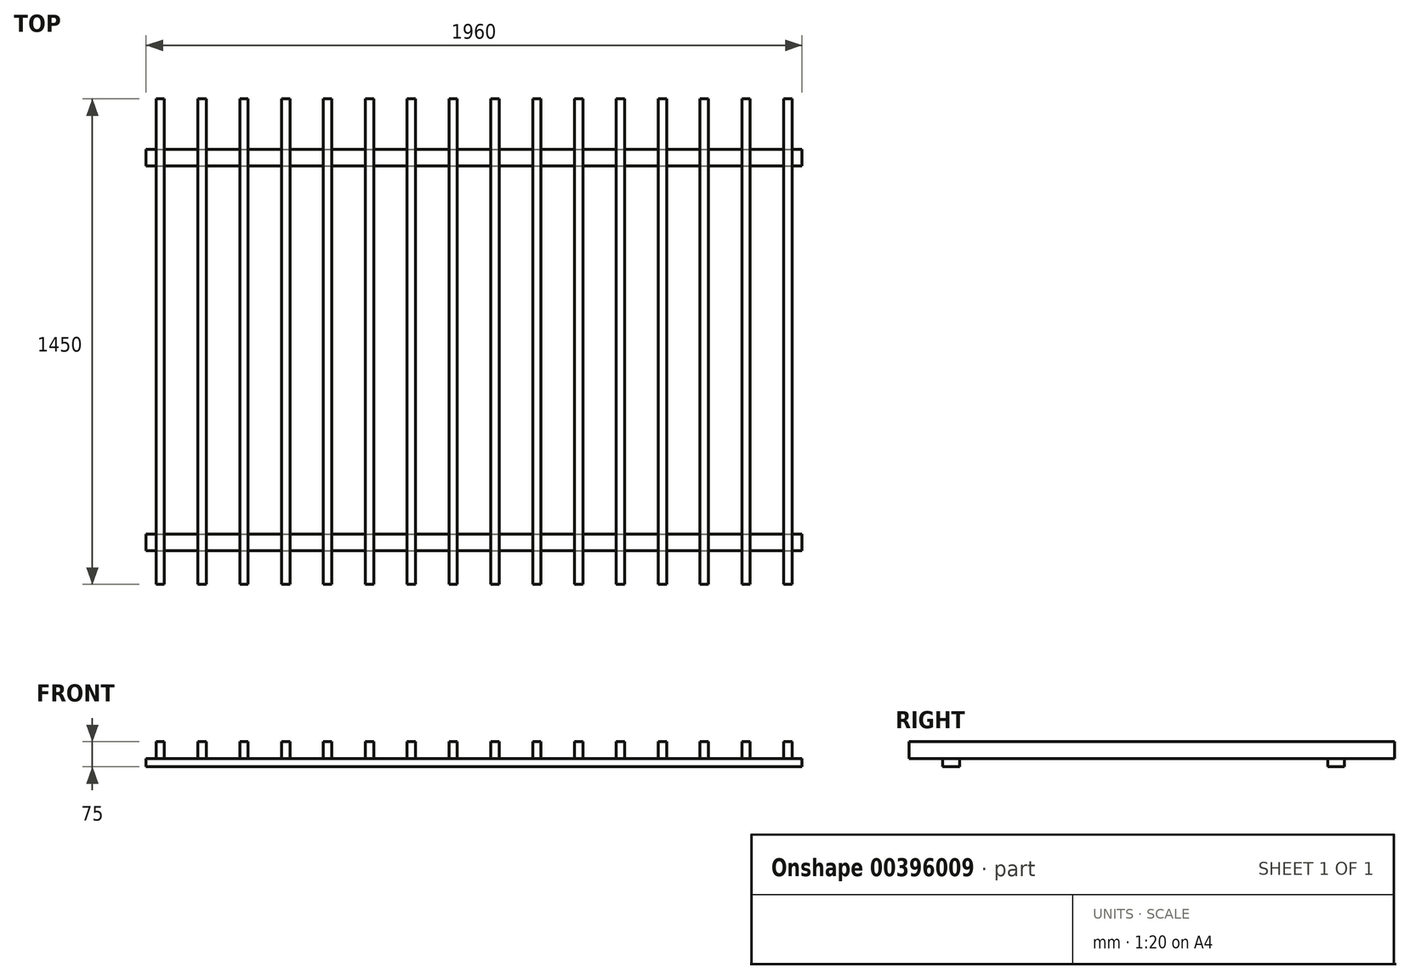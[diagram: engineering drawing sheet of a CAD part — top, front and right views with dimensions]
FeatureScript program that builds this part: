
annotation { "Feature Type Name" : "Feature", "Feature Type Description" : "" }
export const myFeature = defineFeature(function(context is Context, id is Id, definition is map)
    precondition{}
    {
        {
            var Q0;
            Q0=qCreatedBy(makeId("Top.planeOp"),FACE);
            var sketch = newSketch(context, id + "F0", { "sketchPlane" : qUnion([Q0])});
            skLineSegment(sketch, "E0.bottom", {"start": v(0, 0) * mm, "end": v(1960, 0) * mm, "construction": true});
            skLineSegment(sketch, "E0.top", {"start": v(0, 1500) * mm, "end": v(1960, 1500) * mm, "construction": true});
            skLineSegment(sketch, "E0.left", {"start": v(0, 0) * mm, "end": v(0, 1500) * mm, "construction": true});
            skLineSegment(sketch, "E0.right", {"start": v(1960, 0) * mm, "end": v(1960, 1500) * mm, "construction": true});
            skLineSegment(sketch, "E1.bottom", {"start": v(0, 150) * mm, "end": v(1960, 150) * mm});
            skLineSegment(sketch, "E1.top", {"start": v(0, 175) * mm, "end": v(1960, 175) * mm});
            skLineSegment(sketch, "E1.left", {"start": v(0, 150) * mm, "end": v(0, 175) * mm});
            skLineSegment(sketch, "E1.right", {"start": v(1960, 150) * mm, "end": v(1960, 175) * mm});
            skLineSegment(sketch, "E2", {"start": v(0, 750) * mm, "end": v(1960, 750) * mm, "construction": true});
            skLineSegment(sketch, "E3.MirrorCS", {"start": v(1960, 1350) * mm, "end": v(1960, 1325) * mm});
            skLineSegment(sketch, "E4.MirrorCS", {"start": v(0, 1350) * mm, "end": v(0, 1325) * mm});
            skLineSegment(sketch, "E5.MirrorCS", {"start": v(0, 1350) * mm, "end": v(1960, 1350) * mm});
            skLineSegment(sketch, "E6.MirrorCS", {"start": v(0, 1325) * mm, "end": v(1960, 1325) * mm});
            skLineSegment(sketch, "E7.bottom", {"start": v(30, 1500) * mm, "end": v(55, 1500) * mm});
            skLineSegment(sketch, "E7.top", {"start": v(30, 50) * mm, "end": v(55, 50) * mm});
            skLineSegment(sketch, "E7.left", {"start": v(30, 1500) * mm, "end": v(30, 50) * mm});
            skLineSegment(sketch, "E7.right", {"start": v(55, 1500) * mm, "end": v(55, 50) * mm});
            skLineSegment(sketch, "E8.1.0.0", {"start": v(155, 1500) * mm, "end": v(155, 50) * mm});
            skLineSegment(sketch, "E8.1.0.1", {"start": v(180, 1500) * mm, "end": v(180, 50) * mm});
            skLineSegment(sketch, "E8.1.0.2", {"start": v(155, 1500) * mm, "end": v(180, 1500) * mm});
            skLineSegment(sketch, "E8.1.0.3", {"start": v(155, 50) * mm, "end": v(180, 50) * mm});
            skLineSegment(sketch, "E8.2.0.0", {"start": v(280, 1500) * mm, "end": v(280, 50) * mm});
            skLineSegment(sketch, "E8.2.0.1", {"start": v(305, 1500) * mm, "end": v(305, 50) * mm});
            skLineSegment(sketch, "E8.2.0.2", {"start": v(280, 1500) * mm, "end": v(305, 1500) * mm});
            skLineSegment(sketch, "E8.2.0.3", {"start": v(280, 50) * mm, "end": v(305, 50) * mm});
            skLineSegment(sketch, "E8.3.0.0", {"start": v(405, 1500) * mm, "end": v(405, 50) * mm});
            skLineSegment(sketch, "E8.3.0.1", {"start": v(430, 1500) * mm, "end": v(430, 50) * mm});
            skLineSegment(sketch, "E8.3.0.2", {"start": v(405, 1500) * mm, "end": v(430, 1500) * mm});
            skLineSegment(sketch, "E8.3.0.3", {"start": v(405, 50) * mm, "end": v(430, 50) * mm});
            skLineSegment(sketch, "E8.4.0.0", {"start": v(530, 1500) * mm, "end": v(530, 50) * mm});
            skLineSegment(sketch, "E8.4.0.1", {"start": v(555, 1500) * mm, "end": v(555, 50) * mm});
            skLineSegment(sketch, "E8.4.0.2", {"start": v(530, 1500) * mm, "end": v(555, 1500) * mm});
            skLineSegment(sketch, "E8.4.0.3", {"start": v(530, 50) * mm, "end": v(555, 50) * mm});
            skLineSegment(sketch, "E8.5.0.0", {"start": v(655, 1500) * mm, "end": v(655, 50) * mm});
            skLineSegment(sketch, "E8.5.0.1", {"start": v(680, 1500) * mm, "end": v(680, 50) * mm});
            skLineSegment(sketch, "E8.5.0.2", {"start": v(655, 1500) * mm, "end": v(680, 1500) * mm});
            skLineSegment(sketch, "E8.5.0.3", {"start": v(655, 50) * mm, "end": v(680, 50) * mm});
            skLineSegment(sketch, "E8.6.0.0", {"start": v(780, 1500) * mm, "end": v(780, 50) * mm});
            skLineSegment(sketch, "E8.6.0.1", {"start": v(805, 1500) * mm, "end": v(805, 50) * mm});
            skLineSegment(sketch, "E8.6.0.2", {"start": v(780, 1500) * mm, "end": v(805, 1500) * mm});
            skLineSegment(sketch, "E8.6.0.3", {"start": v(780, 50) * mm, "end": v(805, 50) * mm});
            skLineSegment(sketch, "E8.7.0.0", {"start": v(905, 1500) * mm, "end": v(905, 50) * mm});
            skLineSegment(sketch, "E8.7.0.1", {"start": v(930, 1500) * mm, "end": v(930, 50) * mm});
            skLineSegment(sketch, "E8.7.0.2", {"start": v(905, 1500) * mm, "end": v(930, 1500) * mm});
            skLineSegment(sketch, "E8.7.0.3", {"start": v(905, 50) * mm, "end": v(930, 50) * mm});
            skLineSegment(sketch, "E8.8.0.0", {"start": v(1030, 1500) * mm, "end": v(1030, 50) * mm});
            skLineSegment(sketch, "E8.8.0.1", {"start": v(1055, 1500) * mm, "end": v(1055, 50) * mm});
            skLineSegment(sketch, "E8.8.0.2", {"start": v(1030, 1500) * mm, "end": v(1055, 1500) * mm});
            skLineSegment(sketch, "E8.8.0.3", {"start": v(1030, 50) * mm, "end": v(1055, 50) * mm});
            skLineSegment(sketch, "E8.9.0.0", {"start": v(1155, 1500) * mm, "end": v(1155, 50) * mm});
            skLineSegment(sketch, "E8.9.0.1", {"start": v(1180, 1500) * mm, "end": v(1180, 50) * mm});
            skLineSegment(sketch, "E8.9.0.2", {"start": v(1155, 1500) * mm, "end": v(1180, 1500) * mm});
            skLineSegment(sketch, "E8.9.0.3", {"start": v(1155, 50) * mm, "end": v(1180, 50) * mm});
            skLineSegment(sketch, "E8.10.0.0", {"start": v(1280, 1500) * mm, "end": v(1280, 50) * mm});
            skLineSegment(sketch, "E8.10.0.1", {"start": v(1305, 1500) * mm, "end": v(1305, 50) * mm});
            skLineSegment(sketch, "E8.10.0.2", {"start": v(1280, 1500) * mm, "end": v(1305, 1500) * mm});
            skLineSegment(sketch, "E8.10.0.3", {"start": v(1280, 50) * mm, "end": v(1305, 50) * mm});
            skLineSegment(sketch, "E8.11.0.0", {"start": v(1405, 1500) * mm, "end": v(1405, 50) * mm});
            skLineSegment(sketch, "E8.11.0.1", {"start": v(1430, 1500) * mm, "end": v(1430, 50) * mm});
            skLineSegment(sketch, "E8.11.0.2", {"start": v(1405, 1500) * mm, "end": v(1430, 1500) * mm});
            skLineSegment(sketch, "E8.11.0.3", {"start": v(1405, 50) * mm, "end": v(1430, 50) * mm});
            skLineSegment(sketch, "E8.12.0.0", {"start": v(1530, 1500) * mm, "end": v(1530, 50) * mm});
            skLineSegment(sketch, "E8.12.0.1", {"start": v(1555, 1500) * mm, "end": v(1555, 50) * mm});
            skLineSegment(sketch, "E8.12.0.2", {"start": v(1530, 1500) * mm, "end": v(1555, 1500) * mm});
            skLineSegment(sketch, "E8.12.0.3", {"start": v(1530, 50) * mm, "end": v(1555, 50) * mm});
            skLineSegment(sketch, "E8.13.0.0", {"start": v(1655, 1500) * mm, "end": v(1655, 50) * mm});
            skLineSegment(sketch, "E8.13.0.1", {"start": v(1680, 1500) * mm, "end": v(1680, 50) * mm});
            skLineSegment(sketch, "E8.13.0.2", {"start": v(1655, 1500) * mm, "end": v(1680, 1500) * mm});
            skLineSegment(sketch, "E8.13.0.3", {"start": v(1655, 50) * mm, "end": v(1680, 50) * mm});
            skLineSegment(sketch, "E8.14.0.0", {"start": v(1780, 1500) * mm, "end": v(1780, 50) * mm});
            skLineSegment(sketch, "E8.14.0.1", {"start": v(1805, 1500) * mm, "end": v(1805, 50) * mm});
            skLineSegment(sketch, "E8.14.0.2", {"start": v(1780, 1500) * mm, "end": v(1805, 1500) * mm});
            skLineSegment(sketch, "E8.14.0.3", {"start": v(1780, 50) * mm, "end": v(1805, 50) * mm});
            skLineSegment(sketch, "E8.direction1", {"start": v(30, 50) * mm, "end": v(155, 50) * mm, "construction": true});
            skLineSegment(sketch, "E9.0.15.0", {"start": v(1905, 1500) * mm, "end": v(1905, 50) * mm});
            skLineSegment(sketch, "E9.3.15.0", {"start": v(1930, 1500) * mm, "end": v(1930, 50) * mm});
            skLineSegment(sketch, "E9.6.15.0", {"start": v(1905, 1500) * mm, "end": v(1930, 1500) * mm});
            skLineSegment(sketch, "E9.9.15.0", {"start": v(1905, 50) * mm, "end": v(1930, 50) * mm});
            skSolve(sketch);
        }
        {
            var Q0;
            {var subQ5=sQuery(id+"F0.wireOp",EDGE,"E7.top");Q0=makeQuery(id+"F0.imprint","IMPRINT",FACE,{"disambiguationData":[TD([[makeQuery(id+"F0.imprint","IMPRINT",EDGE,{"derivedFrom":subQ5}),1.0]])]});}
            var Q1;
            {var subQ5=sQuery(id+"F0.wireOp",EDGE,"E8.1.0.3");Q1=makeQuery(id+"F0.imprint","IMPRINT",FACE,{"disambiguationData":[TD([[makeQuery(id+"F0.imprint","IMPRINT",EDGE,{"derivedFrom":subQ5}),1.0]])]});}
            var Q2;
            {var subQ5=sQuery(id+"F0.wireOp",EDGE,"E8.2.0.3");Q2=makeQuery(id+"F0.imprint","IMPRINT",FACE,{"disambiguationData":[TD([[makeQuery(id+"F0.imprint","IMPRINT",EDGE,{"derivedFrom":subQ5}),1.0]])]});}
            var Q3;
            {var subQ5=sQuery(id+"F0.wireOp",EDGE,"E8.3.0.3");Q3=makeQuery(id+"F0.imprint","IMPRINT",FACE,{"disambiguationData":[TD([[makeQuery(id+"F0.imprint","IMPRINT",EDGE,{"derivedFrom":subQ5}),1.0]])]});}
            var Q4;
            {var subQ5=sQuery(id+"F0.wireOp",EDGE,"E8.4.0.3");Q4=makeQuery(id+"F0.imprint","IMPRINT",FACE,{"disambiguationData":[TD([[makeQuery(id+"F0.imprint","IMPRINT",EDGE,{"derivedFrom":subQ5}),1.0]])]});}
            var Q5;
            {var subQ5=sQuery(id+"F0.wireOp",EDGE,"E8.5.0.3");Q5=makeQuery(id+"F0.imprint","IMPRINT",FACE,{"disambiguationData":[TD([[makeQuery(id+"F0.imprint","IMPRINT",EDGE,{"derivedFrom":subQ5}),1.0]])]});}
            var Q6;
            {var subQ5=sQuery(id+"F0.wireOp",EDGE,"E8.6.0.3");Q6=makeQuery(id+"F0.imprint","IMPRINT",FACE,{"disambiguationData":[TD([[makeQuery(id+"F0.imprint","IMPRINT",EDGE,{"derivedFrom":subQ5}),1.0]])]});}
            var Q7;
            {var subQ5=sQuery(id+"F0.wireOp",EDGE,"E8.7.0.3");Q7=makeQuery(id+"F0.imprint","IMPRINT",FACE,{"disambiguationData":[TD([[makeQuery(id+"F0.imprint","IMPRINT",EDGE,{"derivedFrom":subQ5}),1.0]])]});}
            var Q8;
            {var subQ5=sQuery(id+"F0.wireOp",EDGE,"E8.8.0.3");Q8=makeQuery(id+"F0.imprint","IMPRINT",FACE,{"disambiguationData":[TD([[makeQuery(id+"F0.imprint","IMPRINT",EDGE,{"derivedFrom":subQ5}),1.0]])]});}
            var Q9;
            {var subQ5=sQuery(id+"F0.wireOp",EDGE,"E8.9.0.3");Q9=makeQuery(id+"F0.imprint","IMPRINT",FACE,{"disambiguationData":[TD([[makeQuery(id+"F0.imprint","IMPRINT",EDGE,{"derivedFrom":subQ5}),1.0]])]});}
            var Q10;
            {var subQ5=sQuery(id+"F0.wireOp",EDGE,"E8.10.0.3");Q10=makeQuery(id+"F0.imprint","IMPRINT",FACE,{"disambiguationData":[TD([[makeQuery(id+"F0.imprint","IMPRINT",EDGE,{"derivedFrom":subQ5}),1.0]])]});}
            var Q11;
            {var subQ5=sQuery(id+"F0.wireOp",EDGE,"E8.11.0.3");Q11=makeQuery(id+"F0.imprint","IMPRINT",FACE,{"disambiguationData":[TD([[makeQuery(id+"F0.imprint","IMPRINT",EDGE,{"derivedFrom":subQ5}),1.0]])]});}
            var Q12;
            {var subQ5=sQuery(id+"F0.wireOp",EDGE,"E8.12.0.3");Q12=makeQuery(id+"F0.imprint","IMPRINT",FACE,{"disambiguationData":[TD([[makeQuery(id+"F0.imprint","IMPRINT",EDGE,{"derivedFrom":subQ5}),1.0]])]});}
            var Q13;
            {var subQ5=sQuery(id+"F0.wireOp",EDGE,"E8.13.0.3");Q13=makeQuery(id+"F0.imprint","IMPRINT",FACE,{"disambiguationData":[TD([[makeQuery(id+"F0.imprint","IMPRINT",EDGE,{"derivedFrom":subQ5}),1.0]])]});}
            var Q14;
            {var subQ5=sQuery(id+"F0.wireOp",EDGE,"E8.14.0.3");Q14=makeQuery(id+"F0.imprint","IMPRINT",FACE,{"disambiguationData":[TD([[makeQuery(id+"F0.imprint","IMPRINT",EDGE,{"derivedFrom":subQ5}),1.0]])]});}
            var Q15;
            {var subQ5=sQuery(id+"F0.wireOp",EDGE,"E9.9.15.0");Q15=makeQuery(id+"F0.imprint","IMPRINT",FACE,{"disambiguationData":[TD([[makeQuery(id+"F0.imprint","IMPRINT",EDGE,{"derivedFrom":subQ5}),1.0]])]});}
            var Q16;
            {var subQ5=sQuery(id+"F0.wireOp",EDGE,"E7.bottom");Q16=makeQuery(id+"F0.imprint","IMPRINT",FACE,{"disambiguationData":[TD([[makeQuery(id+"F0.imprint","IMPRINT",EDGE,{"derivedFrom":subQ5}),-1.0]])]});}
            var Q17;
            {var subQ5=sQuery(id+"F0.wireOp",EDGE,"E8.1.0.2");Q17=makeQuery(id+"F0.imprint","IMPRINT",FACE,{"disambiguationData":[TD([[makeQuery(id+"F0.imprint","IMPRINT",EDGE,{"derivedFrom":subQ5}),-1.0]])]});}
            var Q18;
            {var subQ5=sQuery(id+"F0.wireOp",EDGE,"E8.2.0.2");Q18=makeQuery(id+"F0.imprint","IMPRINT",FACE,{"disambiguationData":[TD([[makeQuery(id+"F0.imprint","IMPRINT",EDGE,{"derivedFrom":subQ5}),-1.0]])]});}
            var Q19;
            {var subQ5=sQuery(id+"F0.wireOp",EDGE,"E8.3.0.2");Q19=makeQuery(id+"F0.imprint","IMPRINT",FACE,{"disambiguationData":[TD([[makeQuery(id+"F0.imprint","IMPRINT",EDGE,{"derivedFrom":subQ5}),-1.0]])]});}
            var Q20;
            {var subQ5=sQuery(id+"F0.wireOp",EDGE,"E8.4.0.2");Q20=makeQuery(id+"F0.imprint","IMPRINT",FACE,{"disambiguationData":[TD([[makeQuery(id+"F0.imprint","IMPRINT",EDGE,{"derivedFrom":subQ5}),-1.0]])]});}
            var Q21;
            {var subQ5=sQuery(id+"F0.wireOp",EDGE,"E8.5.0.2");Q21=makeQuery(id+"F0.imprint","IMPRINT",FACE,{"disambiguationData":[TD([[makeQuery(id+"F0.imprint","IMPRINT",EDGE,{"derivedFrom":subQ5}),-1.0]])]});}
            var Q22;
            {var subQ5=sQuery(id+"F0.wireOp",EDGE,"E8.6.0.2");Q22=makeQuery(id+"F0.imprint","IMPRINT",FACE,{"disambiguationData":[TD([[makeQuery(id+"F0.imprint","IMPRINT",EDGE,{"derivedFrom":subQ5}),-1.0]])]});}
            var Q23;
            {var subQ5=sQuery(id+"F0.wireOp",EDGE,"E8.7.0.2");Q23=makeQuery(id+"F0.imprint","IMPRINT",FACE,{"disambiguationData":[TD([[makeQuery(id+"F0.imprint","IMPRINT",EDGE,{"derivedFrom":subQ5}),-1.0]])]});}
            var Q24;
            {var subQ5=sQuery(id+"F0.wireOp",EDGE,"E8.8.0.2");Q24=makeQuery(id+"F0.imprint","IMPRINT",FACE,{"disambiguationData":[TD([[makeQuery(id+"F0.imprint","IMPRINT",EDGE,{"derivedFrom":subQ5}),-1.0]])]});}
            var Q25;
            {var subQ5=sQuery(id+"F0.wireOp",EDGE,"E8.9.0.2");Q25=makeQuery(id+"F0.imprint","IMPRINT",FACE,{"disambiguationData":[TD([[makeQuery(id+"F0.imprint","IMPRINT",EDGE,{"derivedFrom":subQ5}),-1.0]])]});}
            var Q26;
            {var subQ5=sQuery(id+"F0.wireOp",EDGE,"E8.10.0.2");Q26=makeQuery(id+"F0.imprint","IMPRINT",FACE,{"disambiguationData":[TD([[makeQuery(id+"F0.imprint","IMPRINT",EDGE,{"derivedFrom":subQ5}),-1.0]])]});}
            var Q27;
            {var subQ5=sQuery(id+"F0.wireOp",EDGE,"E8.11.0.2");Q27=makeQuery(id+"F0.imprint","IMPRINT",FACE,{"disambiguationData":[TD([[makeQuery(id+"F0.imprint","IMPRINT",EDGE,{"derivedFrom":subQ5}),-1.0]])]});}
            var Q28;
            {var subQ5=sQuery(id+"F0.wireOp",EDGE,"E8.12.0.2");Q28=makeQuery(id+"F0.imprint","IMPRINT",FACE,{"disambiguationData":[TD([[makeQuery(id+"F0.imprint","IMPRINT",EDGE,{"derivedFrom":subQ5}),-1.0]])]});}
            var Q29;
            {var subQ5=sQuery(id+"F0.wireOp",EDGE,"E8.13.0.2");Q29=makeQuery(id+"F0.imprint","IMPRINT",FACE,{"disambiguationData":[TD([[makeQuery(id+"F0.imprint","IMPRINT",EDGE,{"derivedFrom":subQ5}),-1.0]])]});}
            var Q30;
            {var subQ5=sQuery(id+"F0.wireOp",EDGE,"E8.14.0.2");Q30=makeQuery(id+"F0.imprint","IMPRINT",FACE,{"disambiguationData":[TD([[makeQuery(id+"F0.imprint","IMPRINT",EDGE,{"derivedFrom":subQ5}),-1.0]])]});}
            var Q31;
            {var subQ5=sQuery(id+"F0.wireOp",EDGE,"E9.6.15.0");Q31=makeQuery(id+"F0.imprint","IMPRINT",FACE,{"disambiguationData":[TD([[makeQuery(id+"F0.imprint","IMPRINT",EDGE,{"derivedFrom":subQ5}),-1.0]])]});}
            var Q32;
            {var subQ0=sQuery(id+"F0.wireOp",EDGE,"E7.left");var subQ1=sQuery(id+"F0.wireOp",EDGE,"E1.top");var subQ2=makeQuery(id+"F0.imprint","INTERSECT",VERTEX,{"derivedFrom":[subQ1,subQ0]});Q32=makeQuery(id+"F0.imprint","IMPRINT",FACE,{"disambiguationData":[TD([[makeQuery(id+"F0.imprint","IMPRINT",EDGE,{"disambiguationData":[TD([[subQ2,-1.0]])],"derivedFrom":subQ1}),1.0]])]});}
            var Q33;
            {var subQ0=sQuery(id+"F0.wireOp",EDGE,"E9.3.15.0");var subQ1=sQuery(id+"F0.wireOp",EDGE,"E1.top");var subQ2=makeQuery(id+"F0.imprint","INTERSECT",VERTEX,{"derivedFrom":[subQ1,subQ0]});Q33=makeQuery(id+"F0.imprint","IMPRINT",FACE,{"disambiguationData":[TD([[makeQuery(id+"F0.imprint","IMPRINT",EDGE,{"disambiguationData":[TD([[subQ2,1.0]])],"derivedFrom":subQ1}),1.0]])]});}
            var Q34;
            {var subQ0=sQuery(id+"F0.wireOp",EDGE,"E7.left");var subQ1=sQuery(id+"F0.wireOp",EDGE,"E1.bottom");var subQ2=makeQuery(id+"F0.imprint","INTERSECT",VERTEX,{"derivedFrom":[subQ1,subQ0]});Q34=makeQuery(id+"F0.imprint","IMPRINT",FACE,{"disambiguationData":[TD([[makeQuery(id+"F0.imprint","IMPRINT",EDGE,{"disambiguationData":[TD([[subQ2,-1.0]])],"derivedFrom":subQ1}),1.0]])]});}
            var Q35;
            {var subQ0=sQuery(id+"F0.wireOp",EDGE,"E8.1.0.0");var subQ1=sQuery(id+"F0.wireOp",EDGE,"E1.bottom");var subQ2=makeQuery(id+"F0.imprint","INTERSECT",VERTEX,{"derivedFrom":[subQ1,subQ0]});Q35=makeQuery(id+"F0.imprint","IMPRINT",FACE,{"disambiguationData":[TD([[makeQuery(id+"F0.imprint","IMPRINT",EDGE,{"disambiguationData":[TD([[subQ2,-1.0]])],"derivedFrom":subQ1}),1.0]])]});}
            var Q36;
            {var subQ0=sQuery(id+"F0.wireOp",EDGE,"E8.2.0.0");var subQ1=sQuery(id+"F0.wireOp",EDGE,"E1.bottom");var subQ2=makeQuery(id+"F0.imprint","INTERSECT",VERTEX,{"derivedFrom":[subQ1,subQ0]});Q36=makeQuery(id+"F0.imprint","IMPRINT",FACE,{"disambiguationData":[TD([[makeQuery(id+"F0.imprint","IMPRINT",EDGE,{"disambiguationData":[TD([[subQ2,-1.0]])],"derivedFrom":subQ1}),1.0]])]});}
            var Q37;
            {var subQ0=sQuery(id+"F0.wireOp",EDGE,"E8.3.0.0");var subQ1=sQuery(id+"F0.wireOp",EDGE,"E1.bottom");var subQ2=makeQuery(id+"F0.imprint","INTERSECT",VERTEX,{"derivedFrom":[subQ1,subQ0]});Q37=makeQuery(id+"F0.imprint","IMPRINT",FACE,{"disambiguationData":[TD([[makeQuery(id+"F0.imprint","IMPRINT",EDGE,{"disambiguationData":[TD([[subQ2,-1.0]])],"derivedFrom":subQ1}),1.0]])]});}
            var Q38;
            {var subQ0=sQuery(id+"F0.wireOp",EDGE,"E8.4.0.0");var subQ1=sQuery(id+"F0.wireOp",EDGE,"E1.bottom");var subQ2=makeQuery(id+"F0.imprint","INTERSECT",VERTEX,{"derivedFrom":[subQ1,subQ0]});Q38=makeQuery(id+"F0.imprint","IMPRINT",FACE,{"disambiguationData":[TD([[makeQuery(id+"F0.imprint","IMPRINT",EDGE,{"disambiguationData":[TD([[subQ2,-1.0]])],"derivedFrom":subQ1}),1.0]])]});}
            var Q39;
            {var subQ0=sQuery(id+"F0.wireOp",EDGE,"E8.5.0.0");var subQ1=sQuery(id+"F0.wireOp",EDGE,"E1.bottom");var subQ2=makeQuery(id+"F0.imprint","INTERSECT",VERTEX,{"derivedFrom":[subQ1,subQ0]});Q39=makeQuery(id+"F0.imprint","IMPRINT",FACE,{"disambiguationData":[TD([[makeQuery(id+"F0.imprint","IMPRINT",EDGE,{"disambiguationData":[TD([[subQ2,-1.0]])],"derivedFrom":subQ1}),1.0]])]});}
            var Q40;
            {var subQ0=sQuery(id+"F0.wireOp",EDGE,"E8.6.0.0");var subQ1=sQuery(id+"F0.wireOp",EDGE,"E1.bottom");var subQ2=makeQuery(id+"F0.imprint","INTERSECT",VERTEX,{"derivedFrom":[subQ1,subQ0]});Q40=makeQuery(id+"F0.imprint","IMPRINT",FACE,{"disambiguationData":[TD([[makeQuery(id+"F0.imprint","IMPRINT",EDGE,{"disambiguationData":[TD([[subQ2,-1.0]])],"derivedFrom":subQ1}),1.0]])]});}
            var Q41;
            {var subQ0=sQuery(id+"F0.wireOp",EDGE,"E8.7.0.0");var subQ1=sQuery(id+"F0.wireOp",EDGE,"E1.bottom");var subQ2=makeQuery(id+"F0.imprint","INTERSECT",VERTEX,{"derivedFrom":[subQ1,subQ0]});Q41=makeQuery(id+"F0.imprint","IMPRINT",FACE,{"disambiguationData":[TD([[makeQuery(id+"F0.imprint","IMPRINT",EDGE,{"disambiguationData":[TD([[subQ2,-1.0]])],"derivedFrom":subQ1}),1.0]])]});}
            var Q42;
            {var subQ0=sQuery(id+"F0.wireOp",EDGE,"E8.8.0.0");var subQ1=sQuery(id+"F0.wireOp",EDGE,"E1.bottom");var subQ2=makeQuery(id+"F0.imprint","INTERSECT",VERTEX,{"derivedFrom":[subQ1,subQ0]});Q42=makeQuery(id+"F0.imprint","IMPRINT",FACE,{"disambiguationData":[TD([[makeQuery(id+"F0.imprint","IMPRINT",EDGE,{"disambiguationData":[TD([[subQ2,-1.0]])],"derivedFrom":subQ1}),1.0]])]});}
            var Q43;
            {var subQ0=sQuery(id+"F0.wireOp",EDGE,"E8.9.0.0");var subQ1=sQuery(id+"F0.wireOp",EDGE,"E1.bottom");var subQ2=makeQuery(id+"F0.imprint","INTERSECT",VERTEX,{"derivedFrom":[subQ1,subQ0]});Q43=makeQuery(id+"F0.imprint","IMPRINT",FACE,{"disambiguationData":[TD([[makeQuery(id+"F0.imprint","IMPRINT",EDGE,{"disambiguationData":[TD([[subQ2,-1.0]])],"derivedFrom":subQ1}),1.0]])]});}
            var Q44;
            {var subQ0=sQuery(id+"F0.wireOp",EDGE,"E8.10.0.0");var subQ1=sQuery(id+"F0.wireOp",EDGE,"E1.bottom");var subQ2=makeQuery(id+"F0.imprint","INTERSECT",VERTEX,{"derivedFrom":[subQ1,subQ0]});Q44=makeQuery(id+"F0.imprint","IMPRINT",FACE,{"disambiguationData":[TD([[makeQuery(id+"F0.imprint","IMPRINT",EDGE,{"disambiguationData":[TD([[subQ2,-1.0]])],"derivedFrom":subQ1}),1.0]])]});}
            var Q45;
            {var subQ0=sQuery(id+"F0.wireOp",EDGE,"E8.11.0.0");var subQ1=sQuery(id+"F0.wireOp",EDGE,"E1.bottom");var subQ2=makeQuery(id+"F0.imprint","INTERSECT",VERTEX,{"derivedFrom":[subQ1,subQ0]});Q45=makeQuery(id+"F0.imprint","IMPRINT",FACE,{"disambiguationData":[TD([[makeQuery(id+"F0.imprint","IMPRINT",EDGE,{"disambiguationData":[TD([[subQ2,-1.0]])],"derivedFrom":subQ1}),1.0]])]});}
            var Q46;
            {var subQ0=sQuery(id+"F0.wireOp",EDGE,"E8.12.0.0");var subQ1=sQuery(id+"F0.wireOp",EDGE,"E1.bottom");var subQ2=makeQuery(id+"F0.imprint","INTERSECT",VERTEX,{"derivedFrom":[subQ1,subQ0]});Q46=makeQuery(id+"F0.imprint","IMPRINT",FACE,{"disambiguationData":[TD([[makeQuery(id+"F0.imprint","IMPRINT",EDGE,{"disambiguationData":[TD([[subQ2,-1.0]])],"derivedFrom":subQ1}),1.0]])]});}
            var Q47;
            {var subQ0=sQuery(id+"F0.wireOp",EDGE,"E8.13.0.0");var subQ1=sQuery(id+"F0.wireOp",EDGE,"E1.bottom");var subQ2=makeQuery(id+"F0.imprint","INTERSECT",VERTEX,{"derivedFrom":[subQ1,subQ0]});Q47=makeQuery(id+"F0.imprint","IMPRINT",FACE,{"disambiguationData":[TD([[makeQuery(id+"F0.imprint","IMPRINT",EDGE,{"disambiguationData":[TD([[subQ2,-1.0]])],"derivedFrom":subQ1}),1.0]])]});}
            var Q48;
            {var subQ0=sQuery(id+"F0.wireOp",EDGE,"E8.14.0.0");var subQ1=sQuery(id+"F0.wireOp",EDGE,"E1.bottom");var subQ2=makeQuery(id+"F0.imprint","INTERSECT",VERTEX,{"derivedFrom":[subQ1,subQ0]});Q48=makeQuery(id+"F0.imprint","IMPRINT",FACE,{"disambiguationData":[TD([[makeQuery(id+"F0.imprint","IMPRINT",EDGE,{"disambiguationData":[TD([[subQ2,-1.0]])],"derivedFrom":subQ1}),1.0]])]});}
            var Q49;
            {var subQ0=sQuery(id+"F0.wireOp",EDGE,"E9.0.15.0");var subQ1=sQuery(id+"F0.wireOp",EDGE,"E1.bottom");var subQ2=makeQuery(id+"F0.imprint","INTERSECT",VERTEX,{"derivedFrom":[subQ1,subQ0]});Q49=makeQuery(id+"F0.imprint","IMPRINT",FACE,{"disambiguationData":[TD([[makeQuery(id+"F0.imprint","IMPRINT",EDGE,{"disambiguationData":[TD([[subQ2,-1.0]])],"derivedFrom":subQ1}),1.0]])]});}
            var Q50;
            {var subQ0=sQuery(id+"F0.wireOp",EDGE,"E7.left");var subQ1=sQuery(id+"F0.wireOp",EDGE,"E5.MirrorCS");var subQ2=makeQuery(id+"F0.imprint","INTERSECT",VERTEX,{"derivedFrom":[subQ1,subQ0]});Q50=makeQuery(id+"F0.imprint","IMPRINT",FACE,{"disambiguationData":[TD([[makeQuery(id+"F0.imprint","IMPRINT",EDGE,{"disambiguationData":[TD([[subQ2,-1.0]])],"derivedFrom":subQ1}),-1.0]])]});}
            var Q51;
            {var subQ0=sQuery(id+"F0.wireOp",EDGE,"E8.1.0.0");var subQ1=sQuery(id+"F0.wireOp",EDGE,"E5.MirrorCS");var subQ2=makeQuery(id+"F0.imprint","INTERSECT",VERTEX,{"derivedFrom":[subQ1,subQ0]});Q51=makeQuery(id+"F0.imprint","IMPRINT",FACE,{"disambiguationData":[TD([[makeQuery(id+"F0.imprint","IMPRINT",EDGE,{"disambiguationData":[TD([[subQ2,-1.0]])],"derivedFrom":subQ1}),-1.0]])]});}
            var Q52;
            {var subQ0=sQuery(id+"F0.wireOp",EDGE,"E8.2.0.0");var subQ1=sQuery(id+"F0.wireOp",EDGE,"E5.MirrorCS");var subQ2=makeQuery(id+"F0.imprint","INTERSECT",VERTEX,{"derivedFrom":[subQ1,subQ0]});Q52=makeQuery(id+"F0.imprint","IMPRINT",FACE,{"disambiguationData":[TD([[makeQuery(id+"F0.imprint","IMPRINT",EDGE,{"disambiguationData":[TD([[subQ2,-1.0]])],"derivedFrom":subQ1}),-1.0]])]});}
            var Q53;
            {var subQ0=sQuery(id+"F0.wireOp",EDGE,"E8.3.0.0");var subQ1=sQuery(id+"F0.wireOp",EDGE,"E5.MirrorCS");var subQ2=makeQuery(id+"F0.imprint","INTERSECT",VERTEX,{"derivedFrom":[subQ1,subQ0]});Q53=makeQuery(id+"F0.imprint","IMPRINT",FACE,{"disambiguationData":[TD([[makeQuery(id+"F0.imprint","IMPRINT",EDGE,{"disambiguationData":[TD([[subQ2,-1.0]])],"derivedFrom":subQ1}),-1.0]])]});}
            var Q54;
            {var subQ0=sQuery(id+"F0.wireOp",EDGE,"E8.4.0.0");var subQ1=sQuery(id+"F0.wireOp",EDGE,"E5.MirrorCS");var subQ2=makeQuery(id+"F0.imprint","INTERSECT",VERTEX,{"derivedFrom":[subQ1,subQ0]});Q54=makeQuery(id+"F0.imprint","IMPRINT",FACE,{"disambiguationData":[TD([[makeQuery(id+"F0.imprint","IMPRINT",EDGE,{"disambiguationData":[TD([[subQ2,-1.0]])],"derivedFrom":subQ1}),-1.0]])]});}
            var Q55;
            {var subQ0=sQuery(id+"F0.wireOp",EDGE,"E8.5.0.0");var subQ1=sQuery(id+"F0.wireOp",EDGE,"E5.MirrorCS");var subQ2=makeQuery(id+"F0.imprint","INTERSECT",VERTEX,{"derivedFrom":[subQ1,subQ0]});Q55=makeQuery(id+"F0.imprint","IMPRINT",FACE,{"disambiguationData":[TD([[makeQuery(id+"F0.imprint","IMPRINT",EDGE,{"disambiguationData":[TD([[subQ2,-1.0]])],"derivedFrom":subQ1}),-1.0]])]});}
            var Q56;
            {var subQ0=sQuery(id+"F0.wireOp",EDGE,"E8.6.0.0");var subQ1=sQuery(id+"F0.wireOp",EDGE,"E5.MirrorCS");var subQ2=makeQuery(id+"F0.imprint","INTERSECT",VERTEX,{"derivedFrom":[subQ1,subQ0]});Q56=makeQuery(id+"F0.imprint","IMPRINT",FACE,{"disambiguationData":[TD([[makeQuery(id+"F0.imprint","IMPRINT",EDGE,{"disambiguationData":[TD([[subQ2,-1.0]])],"derivedFrom":subQ1}),-1.0]])]});}
            var Q57;
            {var subQ0=sQuery(id+"F0.wireOp",EDGE,"E8.7.0.0");var subQ1=sQuery(id+"F0.wireOp",EDGE,"E5.MirrorCS");var subQ2=makeQuery(id+"F0.imprint","INTERSECT",VERTEX,{"derivedFrom":[subQ1,subQ0]});Q57=makeQuery(id+"F0.imprint","IMPRINT",FACE,{"disambiguationData":[TD([[makeQuery(id+"F0.imprint","IMPRINT",EDGE,{"disambiguationData":[TD([[subQ2,-1.0]])],"derivedFrom":subQ1}),-1.0]])]});}
            var Q58;
            {var subQ0=sQuery(id+"F0.wireOp",EDGE,"E8.8.0.0");var subQ1=sQuery(id+"F0.wireOp",EDGE,"E5.MirrorCS");var subQ2=makeQuery(id+"F0.imprint","INTERSECT",VERTEX,{"derivedFrom":[subQ1,subQ0]});Q58=makeQuery(id+"F0.imprint","IMPRINT",FACE,{"disambiguationData":[TD([[makeQuery(id+"F0.imprint","IMPRINT",EDGE,{"disambiguationData":[TD([[subQ2,-1.0]])],"derivedFrom":subQ1}),-1.0]])]});}
            var Q59;
            {var subQ0=sQuery(id+"F0.wireOp",EDGE,"E8.9.0.0");var subQ1=sQuery(id+"F0.wireOp",EDGE,"E5.MirrorCS");var subQ2=makeQuery(id+"F0.imprint","INTERSECT",VERTEX,{"derivedFrom":[subQ1,subQ0]});Q59=makeQuery(id+"F0.imprint","IMPRINT",FACE,{"disambiguationData":[TD([[makeQuery(id+"F0.imprint","IMPRINT",EDGE,{"disambiguationData":[TD([[subQ2,-1.0]])],"derivedFrom":subQ1}),-1.0]])]});}
            var Q60;
            {var subQ0=sQuery(id+"F0.wireOp",EDGE,"E8.10.0.0");var subQ1=sQuery(id+"F0.wireOp",EDGE,"E5.MirrorCS");var subQ2=makeQuery(id+"F0.imprint","INTERSECT",VERTEX,{"derivedFrom":[subQ1,subQ0]});Q60=makeQuery(id+"F0.imprint","IMPRINT",FACE,{"disambiguationData":[TD([[makeQuery(id+"F0.imprint","IMPRINT",EDGE,{"disambiguationData":[TD([[subQ2,-1.0]])],"derivedFrom":subQ1}),-1.0]])]});}
            var Q61;
            {var subQ0=sQuery(id+"F0.wireOp",EDGE,"E8.11.0.0");var subQ1=sQuery(id+"F0.wireOp",EDGE,"E5.MirrorCS");var subQ2=makeQuery(id+"F0.imprint","INTERSECT",VERTEX,{"derivedFrom":[subQ1,subQ0]});Q61=makeQuery(id+"F0.imprint","IMPRINT",FACE,{"disambiguationData":[TD([[makeQuery(id+"F0.imprint","IMPRINT",EDGE,{"disambiguationData":[TD([[subQ2,-1.0]])],"derivedFrom":subQ1}),-1.0]])]});}
            var Q62;
            {var subQ0=sQuery(id+"F0.wireOp",EDGE,"E8.12.0.0");var subQ1=sQuery(id+"F0.wireOp",EDGE,"E5.MirrorCS");var subQ2=makeQuery(id+"F0.imprint","INTERSECT",VERTEX,{"derivedFrom":[subQ1,subQ0]});Q62=makeQuery(id+"F0.imprint","IMPRINT",FACE,{"disambiguationData":[TD([[makeQuery(id+"F0.imprint","IMPRINT",EDGE,{"disambiguationData":[TD([[subQ2,-1.0]])],"derivedFrom":subQ1}),-1.0]])]});}
            var Q63;
            {var subQ0=sQuery(id+"F0.wireOp",EDGE,"E8.13.0.0");var subQ1=sQuery(id+"F0.wireOp",EDGE,"E5.MirrorCS");var subQ2=makeQuery(id+"F0.imprint","INTERSECT",VERTEX,{"derivedFrom":[subQ1,subQ0]});Q63=makeQuery(id+"F0.imprint","IMPRINT",FACE,{"disambiguationData":[TD([[makeQuery(id+"F0.imprint","IMPRINT",EDGE,{"disambiguationData":[TD([[subQ2,-1.0]])],"derivedFrom":subQ1}),-1.0]])]});}
            var Q64;
            {var subQ0=sQuery(id+"F0.wireOp",EDGE,"E8.14.0.0");var subQ1=sQuery(id+"F0.wireOp",EDGE,"E5.MirrorCS");var subQ2=makeQuery(id+"F0.imprint","INTERSECT",VERTEX,{"derivedFrom":[subQ1,subQ0]});Q64=makeQuery(id+"F0.imprint","IMPRINT",FACE,{"disambiguationData":[TD([[makeQuery(id+"F0.imprint","IMPRINT",EDGE,{"disambiguationData":[TD([[subQ2,-1.0]])],"derivedFrom":subQ1}),-1.0]])]});}
            var Q65;
            {var subQ0=sQuery(id+"F0.wireOp",EDGE,"E9.0.15.0");var subQ1=sQuery(id+"F0.wireOp",EDGE,"E5.MirrorCS");var subQ2=makeQuery(id+"F0.imprint","INTERSECT",VERTEX,{"derivedFrom":[subQ1,subQ0]});Q65=makeQuery(id+"F0.imprint","IMPRINT",FACE,{"disambiguationData":[TD([[makeQuery(id+"F0.imprint","IMPRINT",EDGE,{"disambiguationData":[TD([[subQ2,-1.0]])],"derivedFrom":subQ1}),-1.0]])]});}
            var Q66;
            {var subQ0=sQuery(id+"F0.wireOp",EDGE,"E8.1.0.0");var subQ1=sQuery(id+"F0.wireOp",EDGE,"E1.top");var subQ2=makeQuery(id+"F0.imprint","INTERSECT",VERTEX,{"derivedFrom":[subQ1,subQ0]});Q66=makeQuery(id+"F0.imprint","IMPRINT",FACE,{"disambiguationData":[TD([[makeQuery(id+"F0.imprint","IMPRINT",EDGE,{"disambiguationData":[TD([[subQ2,-1.0]])],"derivedFrom":subQ1}),1.0]])]});}
            var Q67;
            {var subQ0=sQuery(id+"F0.wireOp",EDGE,"E8.2.0.0");var subQ1=sQuery(id+"F0.wireOp",EDGE,"E1.top");var subQ2=makeQuery(id+"F0.imprint","INTERSECT",VERTEX,{"derivedFrom":[subQ1,subQ0]});Q67=makeQuery(id+"F0.imprint","IMPRINT",FACE,{"disambiguationData":[TD([[makeQuery(id+"F0.imprint","IMPRINT",EDGE,{"disambiguationData":[TD([[subQ2,-1.0]])],"derivedFrom":subQ1}),1.0]])]});}
            var Q68;
            {var subQ0=sQuery(id+"F0.wireOp",EDGE,"E8.3.0.0");var subQ1=sQuery(id+"F0.wireOp",EDGE,"E1.top");var subQ2=makeQuery(id+"F0.imprint","INTERSECT",VERTEX,{"derivedFrom":[subQ1,subQ0]});Q68=makeQuery(id+"F0.imprint","IMPRINT",FACE,{"disambiguationData":[TD([[makeQuery(id+"F0.imprint","IMPRINT",EDGE,{"disambiguationData":[TD([[subQ2,-1.0]])],"derivedFrom":subQ1}),1.0]])]});}
            var Q69;
            {var subQ0=sQuery(id+"F0.wireOp",EDGE,"E8.4.0.0");var subQ1=sQuery(id+"F0.wireOp",EDGE,"E1.top");var subQ2=makeQuery(id+"F0.imprint","INTERSECT",VERTEX,{"derivedFrom":[subQ1,subQ0]});Q69=makeQuery(id+"F0.imprint","IMPRINT",FACE,{"disambiguationData":[TD([[makeQuery(id+"F0.imprint","IMPRINT",EDGE,{"disambiguationData":[TD([[subQ2,-1.0]])],"derivedFrom":subQ1}),1.0]])]});}
            var Q70;
            {var subQ0=sQuery(id+"F0.wireOp",EDGE,"E8.5.0.0");var subQ1=sQuery(id+"F0.wireOp",EDGE,"E1.top");var subQ2=makeQuery(id+"F0.imprint","INTERSECT",VERTEX,{"derivedFrom":[subQ1,subQ0]});Q70=makeQuery(id+"F0.imprint","IMPRINT",FACE,{"disambiguationData":[TD([[makeQuery(id+"F0.imprint","IMPRINT",EDGE,{"disambiguationData":[TD([[subQ2,-1.0]])],"derivedFrom":subQ1}),1.0]])]});}
            var Q71;
            {var subQ0=sQuery(id+"F0.wireOp",EDGE,"E8.6.0.0");var subQ1=sQuery(id+"F0.wireOp",EDGE,"E1.top");var subQ2=makeQuery(id+"F0.imprint","INTERSECT",VERTEX,{"derivedFrom":[subQ1,subQ0]});Q71=makeQuery(id+"F0.imprint","IMPRINT",FACE,{"disambiguationData":[TD([[makeQuery(id+"F0.imprint","IMPRINT",EDGE,{"disambiguationData":[TD([[subQ2,-1.0]])],"derivedFrom":subQ1}),1.0]])]});}
            var Q72;
            {var subQ0=sQuery(id+"F0.wireOp",EDGE,"E8.7.0.0");var subQ1=sQuery(id+"F0.wireOp",EDGE,"E1.top");var subQ2=makeQuery(id+"F0.imprint","INTERSECT",VERTEX,{"derivedFrom":[subQ1,subQ0]});Q72=makeQuery(id+"F0.imprint","IMPRINT",FACE,{"disambiguationData":[TD([[makeQuery(id+"F0.imprint","IMPRINT",EDGE,{"disambiguationData":[TD([[subQ2,-1.0]])],"derivedFrom":subQ1}),1.0]])]});}
            var Q73;
            {var subQ0=sQuery(id+"F0.wireOp",EDGE,"E8.8.0.0");var subQ1=sQuery(id+"F0.wireOp",EDGE,"E1.top");var subQ2=makeQuery(id+"F0.imprint","INTERSECT",VERTEX,{"derivedFrom":[subQ1,subQ0]});Q73=makeQuery(id+"F0.imprint","IMPRINT",FACE,{"disambiguationData":[TD([[makeQuery(id+"F0.imprint","IMPRINT",EDGE,{"disambiguationData":[TD([[subQ2,-1.0]])],"derivedFrom":subQ1}),1.0]])]});}
            var Q74;
            {var subQ0=sQuery(id+"F0.wireOp",EDGE,"E8.9.0.0");var subQ1=sQuery(id+"F0.wireOp",EDGE,"E1.top");var subQ2=makeQuery(id+"F0.imprint","INTERSECT",VERTEX,{"derivedFrom":[subQ1,subQ0]});Q74=makeQuery(id+"F0.imprint","IMPRINT",FACE,{"disambiguationData":[TD([[makeQuery(id+"F0.imprint","IMPRINT",EDGE,{"disambiguationData":[TD([[subQ2,-1.0]])],"derivedFrom":subQ1}),1.0]])]});}
            var Q75;
            {var subQ0=sQuery(id+"F0.wireOp",EDGE,"E8.10.0.0");var subQ1=sQuery(id+"F0.wireOp",EDGE,"E1.top");var subQ2=makeQuery(id+"F0.imprint","INTERSECT",VERTEX,{"derivedFrom":[subQ1,subQ0]});Q75=makeQuery(id+"F0.imprint","IMPRINT",FACE,{"disambiguationData":[TD([[makeQuery(id+"F0.imprint","IMPRINT",EDGE,{"disambiguationData":[TD([[subQ2,-1.0]])],"derivedFrom":subQ1}),1.0]])]});}
            var Q76;
            {var subQ0=sQuery(id+"F0.wireOp",EDGE,"E8.11.0.0");var subQ1=sQuery(id+"F0.wireOp",EDGE,"E1.top");var subQ2=makeQuery(id+"F0.imprint","INTERSECT",VERTEX,{"derivedFrom":[subQ1,subQ0]});Q76=makeQuery(id+"F0.imprint","IMPRINT",FACE,{"disambiguationData":[TD([[makeQuery(id+"F0.imprint","IMPRINT",EDGE,{"disambiguationData":[TD([[subQ2,-1.0]])],"derivedFrom":subQ1}),1.0]])]});}
            var Q77;
            {var subQ0=sQuery(id+"F0.wireOp",EDGE,"E8.12.0.0");var subQ1=sQuery(id+"F0.wireOp",EDGE,"E1.top");var subQ2=makeQuery(id+"F0.imprint","INTERSECT",VERTEX,{"derivedFrom":[subQ1,subQ0]});Q77=makeQuery(id+"F0.imprint","IMPRINT",FACE,{"disambiguationData":[TD([[makeQuery(id+"F0.imprint","IMPRINT",EDGE,{"disambiguationData":[TD([[subQ2,-1.0]])],"derivedFrom":subQ1}),1.0]])]});}
            var Q78;
            {var subQ0=sQuery(id+"F0.wireOp",EDGE,"E8.13.0.0");var subQ1=sQuery(id+"F0.wireOp",EDGE,"E1.top");var subQ2=makeQuery(id+"F0.imprint","INTERSECT",VERTEX,{"derivedFrom":[subQ1,subQ0]});Q78=makeQuery(id+"F0.imprint","IMPRINT",FACE,{"disambiguationData":[TD([[makeQuery(id+"F0.imprint","IMPRINT",EDGE,{"disambiguationData":[TD([[subQ2,-1.0]])],"derivedFrom":subQ1}),1.0]])]});}
            var Q79;
            {var subQ0=sQuery(id+"F0.wireOp",EDGE,"E8.14.0.0");var subQ1=sQuery(id+"F0.wireOp",EDGE,"E1.top");var subQ2=makeQuery(id+"F0.imprint","INTERSECT",VERTEX,{"derivedFrom":[subQ1,subQ0]});Q79=makeQuery(id+"F0.imprint","IMPRINT",FACE,{"disambiguationData":[TD([[makeQuery(id+"F0.imprint","IMPRINT",EDGE,{"disambiguationData":[TD([[subQ2,-1.0]])],"derivedFrom":subQ1}),1.0]])]});}
            extrude(context, id + "F1", {"entities" : qUnion([Q0, Q1, Q2, Q3, Q4, Q5, Q6, Q7, Q8, Q9, Q10, Q11, Q12, Q13, Q14, Q15, Q16, Q17, Q18, Q19, Q20, Q21, Q22, Q23, Q24, Q25, Q26, Q27, Q28, Q29, Q30, Q31, Q32, Q33, Q34, Q35, Q36, Q37, Q38, Q39, Q40, Q41, Q42, Q43, Q44, Q45, Q46, Q47, Q48, Q49, Q50, Q51, Q52, Q53, Q54, Q55, Q56, Q57, Q58, Q59, Q60, Q61, Q62, Q63, Q64, Q65, Q66, Q67, Q68, Q69, Q70, Q71, Q72, Q73, Q74, Q75, Q76, Q77, Q78, Q79]), "depth" : 50 * mm});
        }
        {
            var Q0;
            Q0=qCreatedBy(makeId("Top.planeOp"),FACE);
            var sketch = newSketch(context, id + "F2", { "sketchPlane" : qUnion([Q0])});
            skLineSegment(sketch, "E10.bottom", {"start": v(0, 0) * mm, "end": v(1960, 0) * mm, "construction": true});
            skLineSegment(sketch, "E10.top", {"start": v(0, 1500) * mm, "end": v(1960, 1500) * mm, "construction": true});
            skLineSegment(sketch, "E10.left", {"start": v(0, 0) * mm, "end": v(0, 1500) * mm, "construction": true});
            skLineSegment(sketch, "E10.right", {"start": v(1960, 0) * mm, "end": v(1960, 1500) * mm, "construction": true});
            skLineSegment(sketch, "E11", {"start": v(0, 750) * mm, "end": v(1960, 750) * mm, "construction": true});
            skLineSegment(sketch, "E12.bottom", {"start": v(0, 200) * mm, "end": v(1960, 200) * mm});
            skLineSegment(sketch, "E12.top", {"start": v(0, 150) * mm, "end": v(1960, 150) * mm});
            skLineSegment(sketch, "E12.left", {"start": v(0, 200) * mm, "end": v(0, 150) * mm});
            skLineSegment(sketch, "E12.right", {"start": v(1960, 200) * mm, "end": v(1960, 150) * mm});
            skLineSegment(sketch, "E13.MirrorCS", {"start": v(0, 1300) * mm, "end": v(0, 1350) * mm});
            skLineSegment(sketch, "E14.MirrorCS", {"start": v(1960, 1300) * mm, "end": v(1960, 1350) * mm});
            skLineSegment(sketch, "E15.MirrorCS", {"start": v(0, 1300) * mm, "end": v(1960, 1300) * mm});
            skLineSegment(sketch, "E16.MirrorCS", {"start": v(0, 1350) * mm, "end": v(1960, 1350) * mm});
            skSolve(sketch);
        }
        {
            var Q0;
            Q0 = qSketchRegion(id + "F2", true);
            extrude(context, id + "F3", {"entities" : qUnion([Q0]), "oppositeDirection" : true, "depth" : 25 * mm});
        }
    });
